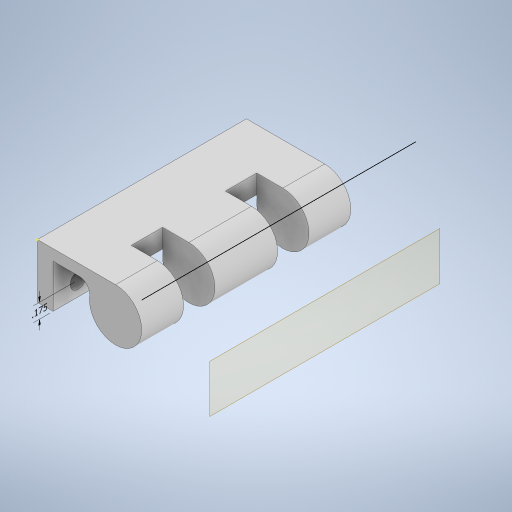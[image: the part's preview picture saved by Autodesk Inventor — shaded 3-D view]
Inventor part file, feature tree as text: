
AUTODESK INVENTOR PART (.ipt)
format: ipt  version: 2024.2 (Build 282272000, 272)  size: 325,120 bytes
history: native  units: in
note: dims shown in document units (in); Inventor stores cm internally (conversion verified against a paired STEP export)
features: sketch x5, extrude x4, other x2, plane x1
ambient origin geometry x8: Origin, YZ Plane, XZ Plane, XY Plane, X Axis, Y Axis, Z Axis, Center Point
bodies: Solid1 (feature_tree)
feature tree (12):
  other  "Annotations"
  extrude  "Extrusion1"  Depth=0.65in
  extrude  "Extrusion2"  Depth=0.3937in
  extrude  "Extrusion3"  Depth=0.13in
  sketch  "Sketch4"  dims[d15=0.04in d16=0.0in d17=0.935in]
  plane  "Work Plane1"
  extrude  "Extrusion4"  Depth=0.935in
  sketch  "Sketch1"  dims[d0=2.5in d1=0.65in]
  sketch  "Sketch2"  dims[d4=2.7559in d6=0.3149in d7=0.3937in d9=1.0in d11=0.3in]
  sketch  "Sketch3"  dims[d12=0.1875in d13=0.0in d14=0.13in]
  sketch  "Sketch6"  dims[d18=0.625in d19=0.125in d20=2.5in d21=0.0in d25=2.0in d26=0.375in d27=0.5in d28=0.375in d29=0.5in d30=0.0in d31=0.0in d32=0.625in d33=0.625in d23=0.0278in d24=0.175in]
  other  "Linear Dimension 1"
